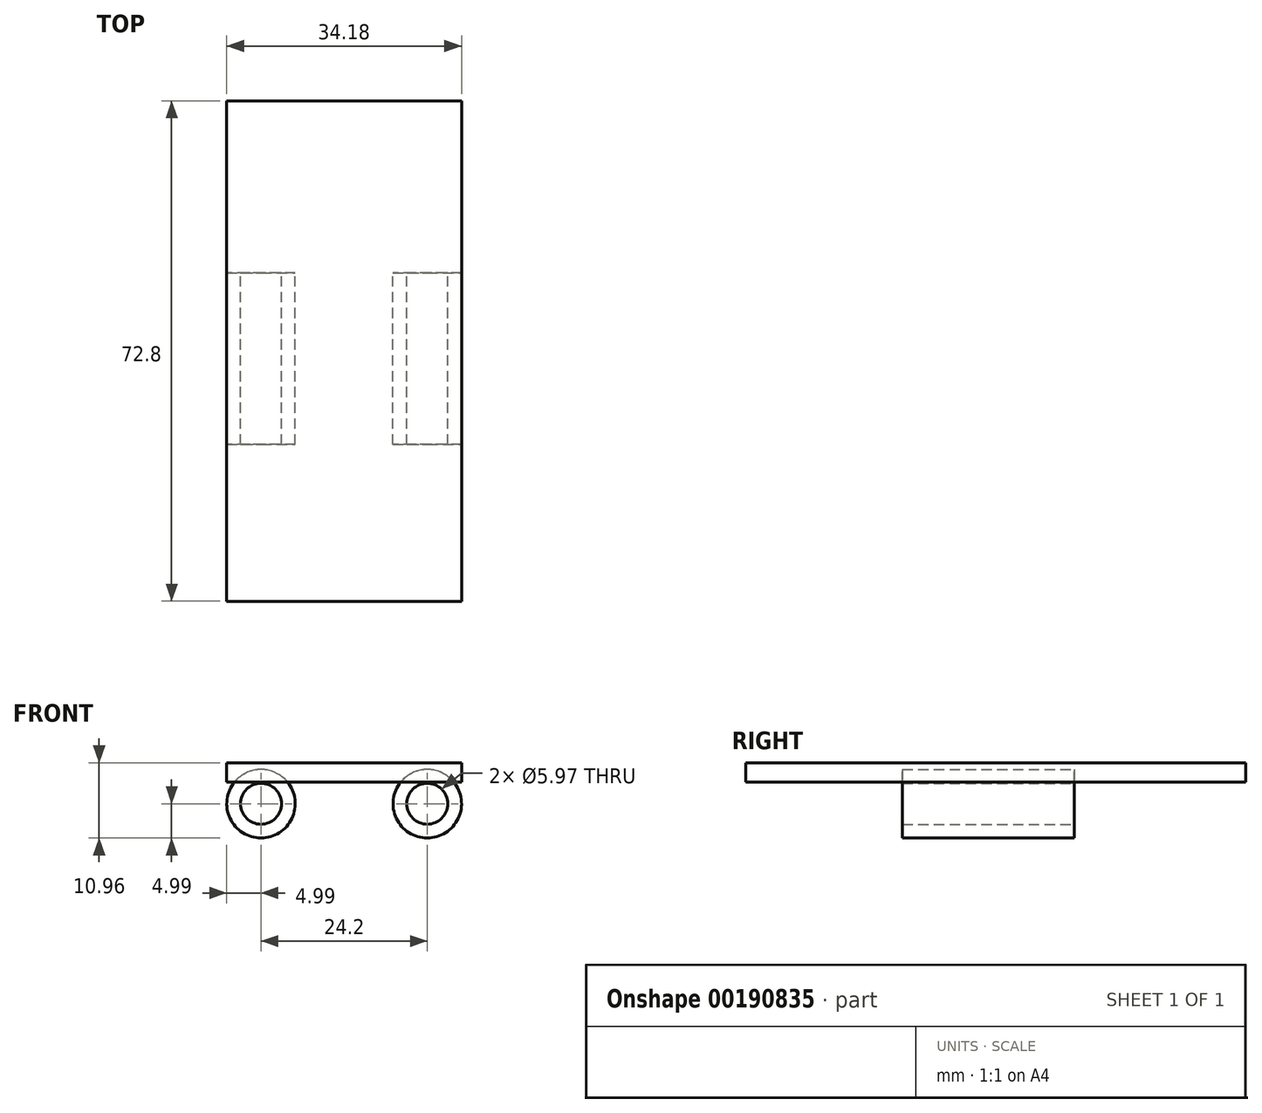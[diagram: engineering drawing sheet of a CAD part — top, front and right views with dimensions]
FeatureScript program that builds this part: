
annotation { "Feature Type Name" : "Feature", "Feature Type Description" : "" }
export const myFeature = defineFeature(function(context is Context, id is Id, definition is map)
    precondition{}
    {
        {
            var Q0;
            Q0=qCreatedBy(makeId("Front.planeOp"),FACE);
            var sketch = newSketch(context, id + "F0", { "sketchPlane" : qUnion([Q0])});
            skCircle(sketch, "E0", {"center": v(0, 0) * mm, "radius": 2.98 * mm});
            skCircle(sketch, "E1.0", {"center": v(0, 0) * mm, "radius": 4.98 * mm});
            skSolve(sketch);
        }
        {
            var Q0;
            Q0 = qSketchRegion(id + "F0", true);
            extrude(context, id + "F1", {"entities" : qUnion([Q0]), "depth" : 25 * mm});
        }
        {
            var Q0;
            Q0=makeQuery(id+"F1.opExtrude","SWEPT_BODY",BODY,{"disambiguationData":[OSD([sQuery(id+"F0.wireOp",EDGE,"E0"),sQuery(id+"F0.wireOp",EDGE,"E1.0")])]});
            transform(context, id + "F2", {"entities" : qUnion([Q0]), "transformType" : TransformType.TRANSLATION_3D, "dx" : 24.2 * mm, "dy" : 0 * mm, "dz" : 0 * mm, "makeCopy" : true});
        }
        {
            var Q0;
            Q0=qCreatedBy(makeId("Top.planeOp"),FACE);
            cPlane(context, id + "F3", {"entities" : qUnion([Q0]), "cplaneType" : CPlaneType.OFFSET, "offset" : 4.97 * mm, "width" : 150 * mm, "height" : 150 * mm});
        }
        {
            var Q0;
            Q0=qCreatedBy(id+"F3.planeOp",FACE);
            var sketch = newSketch(context, id + "F4", { "sketchPlane" : qUnion([Q0])});
            skLineSegment(sketch, "E2", {"start": v(4.98, 0) * mm, "end": v(4.98, -25) * mm});
            skLineSegment(sketch, "E3", {"start": v(-4.98, -27.8) * mm, "end": v(-4.98, 0) * mm});
            skLineSegment(sketch, "E4", {"start": v(29.18, 0) * mm, "end": v(29.18, -25) * mm});
            skLineSegment(sketch, "E5", {"start": v(19.21, -25) * mm, "end": v(19.21, 0) * mm});
            skLineSegment(sketch, "E6.bottom", {"start": v(4.98, 0) * mm, "end": v(19.21, 0) * mm});
            skLineSegment(sketch, "E6.top", {"start": v(4.98, -25) * mm, "end": v(19.21, -25) * mm});
            skLineSegment(sketch, "E6.right", {"start": v(19.21, 0) * mm, "end": v(19.21, -25) * mm});
            skLineSegment(sketch, "E7.bottom", {"start": v(19.21, -25) * mm, "end": v(29.19, -25) * mm});
            skLineSegment(sketch, "E7.top", {"start": v(19.21, 0) * mm, "end": v(29.18, 0) * mm});
            skLineSegment(sketch, "E7.left", {"start": v(19.22, -25) * mm, "end": v(19.21, 0) * mm});
            skLineSegment(sketch, "E7.right", {"start": v(29.19, -25) * mm, "end": v(29.18, 0) * mm});
            skLineSegment(sketch, "E8.bottom", {"start": v(4.98, 0) * mm, "end": v(-4.98, 0) * mm});
            skLineSegment(sketch, "E8.top", {"start": v(4.99, -27.8) * mm, "end": v(-4.98, -27.8) * mm});
            skLineSegment(sketch, "E8.left", {"start": v(4.98, 0) * mm, "end": v(4.98, -27.8) * mm});
            skLineSegment(sketch, "E8.right", {"start": v(-4.98, 0) * mm, "end": v(-4.98, -27.8) * mm});
            skLineSegment(sketch, "E9.bottom", {"start": v(-4.98, 0) * mm, "end": v(29.19, 0) * mm});
            skLineSegment(sketch, "E9.top", {"start": v(-4.98, 25) * mm, "end": v(29.19, 25) * mm});
            skLineSegment(sketch, "E9.left", {"start": v(-4.98, 0) * mm, "end": v(-4.98, 25) * mm});
            skLineSegment(sketch, "E9.right", {"start": v(29.19, 0) * mm, "end": v(29.18, 25) * mm});
            skLineSegment(sketch, "E10.bottom", {"start": v(-4.98, -27.8) * mm, "end": v(29.18, -27.8) * mm});
            skLineSegment(sketch, "E10.top", {"start": v(-4.98, -47.8) * mm, "end": v(29.18, -47.8) * mm});
            skLineSegment(sketch, "E10.left", {"start": v(-4.98, -27.8) * mm, "end": v(-4.98, -47.8) * mm});
            skLineSegment(sketch, "E10.right", {"start": v(29.18, -27.8) * mm, "end": v(29.18, -47.8) * mm});
            skLineSegment(sketch, "E11.bottom", {"start": v(4.99, -27.8) * mm, "end": v(29.18, -27.8) * mm});
            skLineSegment(sketch, "E11.top", {"start": v(4.99, -25) * mm, "end": v(29.18, -25) * mm});
            skLineSegment(sketch, "E11.left", {"start": v(4.99, -27.8) * mm, "end": v(4.99, -25) * mm});
            skLineSegment(sketch, "E11.right", {"start": v(29.18, -27.8) * mm, "end": v(29.18, -25) * mm});
            skLineSegment(sketch, "E12.left", {"start": v(4.98, -25) * mm, "end": v(4.98, 0) * mm});
            skSolve(sketch);
        }
        {
            var Q0;
            Q0 = qSketchRegion(id + "F4", true);
            var Q1;
            Q1=makeQuery(id+"F4.imprint","IMPRINT",FACE,{"disambiguationData":[TD([[makeQuery(id+"F4.imprint","IMPRINT",EDGE,{"derivedFrom":sQuery(id+"F4.wireOp",EDGE,"E6.top")}),1.0]])]});
            extrude(context, id + "F5", {"entities" : qUnion([Q0, Q1]), "depth" : 1 * mm, "hasSecondDirection" : true, "secondDirectionOppositeDirection" : true, "secondDirectionDepth" : 1.8 * mm});
        }
    });
